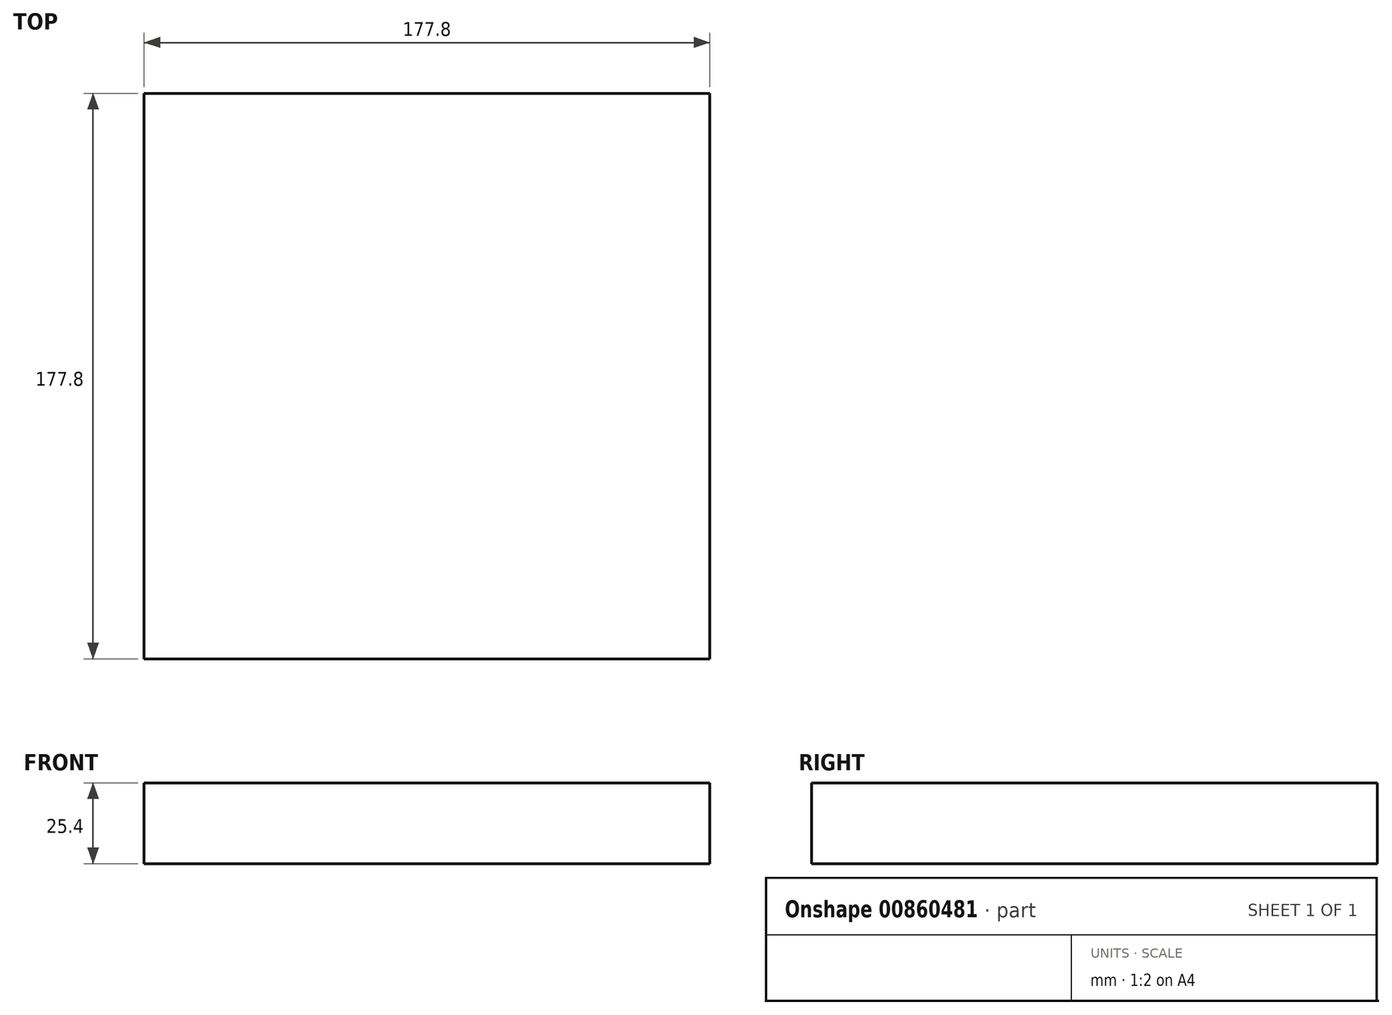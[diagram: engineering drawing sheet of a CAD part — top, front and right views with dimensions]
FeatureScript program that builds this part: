
annotation { "Feature Type Name" : "Feature", "Feature Type Description" : "" }
export const myFeature = defineFeature(function(context is Context, id is Id, definition is map)
    precondition{}
    {
        {
            var Q0;
            Q0=qCreatedBy(makeId("Top.planeOp"),FACE);
            var sketch = newSketch(context, id + "F0", { "sketchPlane" : qUnion([Q0])});
            skLineSegment(sketch, "E0.bottom", {"start": v(88.9, 88.9) * mm, "end": v(-88.9, 88.9) * mm});
            skLineSegment(sketch, "E0.top", {"start": v(88.9, -88.9) * mm, "end": v(-88.9, -88.9) * mm});
            skLineSegment(sketch, "E0.left", {"start": v(88.9, 88.9) * mm, "end": v(88.9, -88.9) * mm});
            skLineSegment(sketch, "E0.right", {"start": v(-88.9, 88.9) * mm, "end": v(-88.9, -88.9) * mm});
            skPoint(sketch, "E0.middle", {"position": v(0, 0) * mm});
            skSolve(sketch);
        }
        {
            var Q0;
            Q0=makeQuery(id+"F0.imprint","IMPRINT",FACE,{"disambiguationData":[TD([[makeQuery(id+"F0.imprint","IMPRINT",EDGE,{"derivedFrom":sQuery(id+"F0.wireOp",EDGE,"E0.bottom")}),1.0]])]});
            extrude(context, id + "F1", {"entities" : qUnion([Q0]), "depth" : 25.4 * mm, "offsetDistance" : 25.4 * mm});
        }
    });
